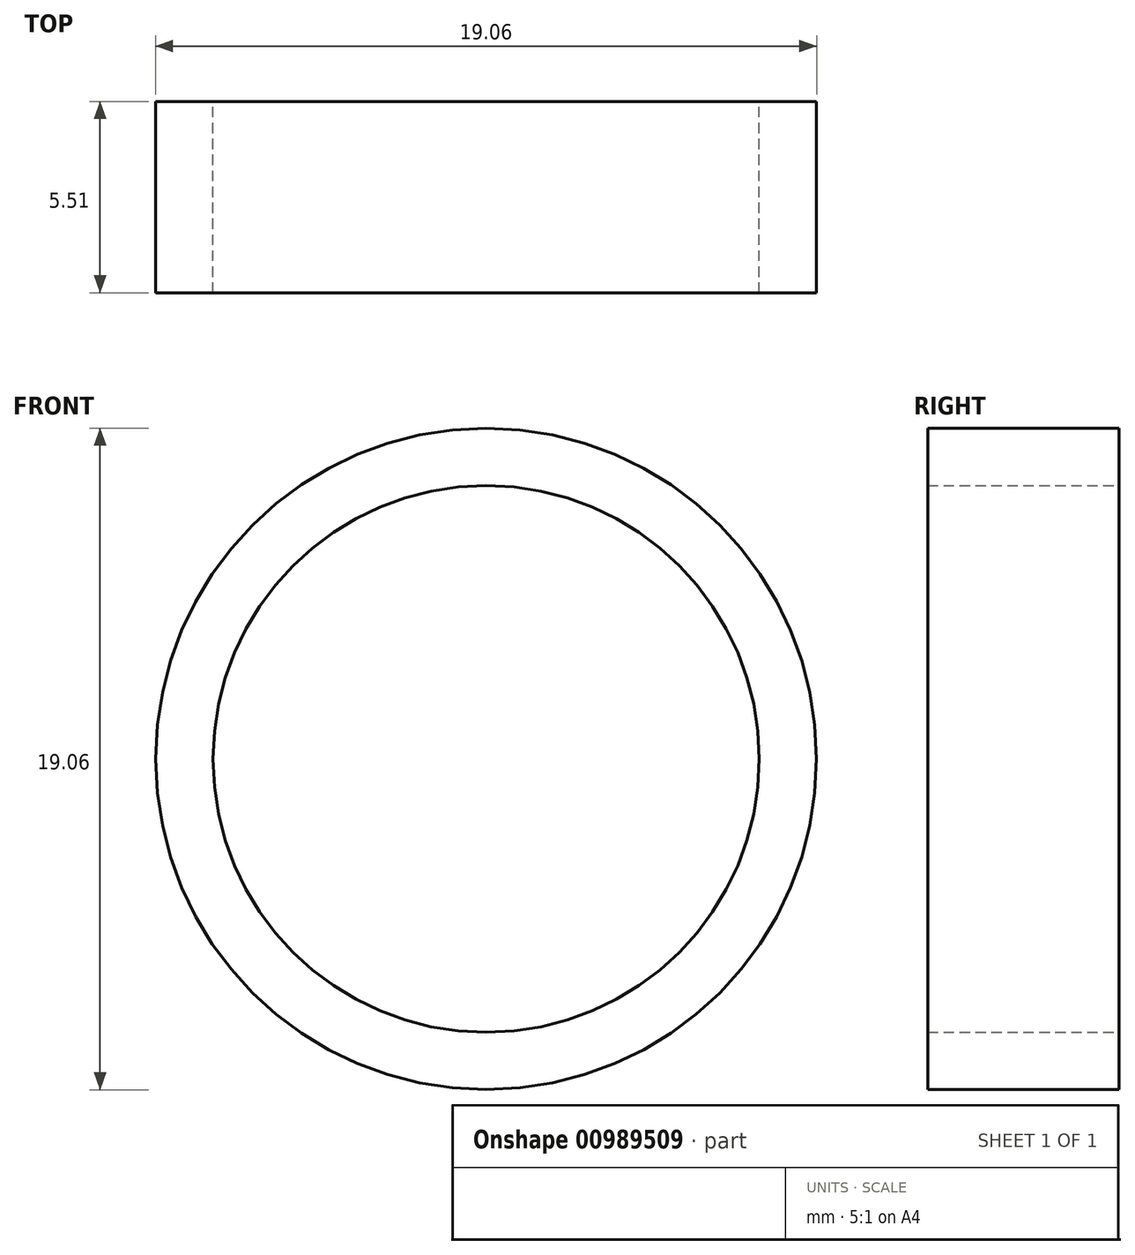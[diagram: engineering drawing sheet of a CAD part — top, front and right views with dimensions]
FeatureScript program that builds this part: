
annotation { "Feature Type Name" : "Feature", "Feature Type Description" : "" }
export const myFeature = defineFeature(function(context is Context, id is Id, definition is map)
    precondition{}
    {
        {
            var Q0;
            Q0=qCreatedBy(makeId("Front.planeOp"),FACE);
            var sketch = newSketch(context, id + "F0", { "sketchPlane" : qUnion([Q0])});
            skCircle(sketch, "E0", {"center": v(0, 0) * mm, "radius": 9.53 * mm});
            skCircle(sketch, "E1", {"center": v(0, 0) * mm, "radius": 7.87 * mm});
            skSolve(sketch);
        }
        {
            var Q0;
            Q0 = qSketchRegion(id + "F0", true);
            extrude(context, id + "F1", {"entities" : qUnion([Q0]), "depth" : 5.5 * mm, "offsetDistance" : 25.4 * mm});
        }
    });
